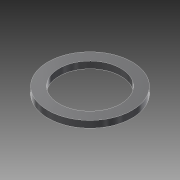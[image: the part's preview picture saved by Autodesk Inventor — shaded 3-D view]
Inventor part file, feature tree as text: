
AUTODESK INVENTOR PART (.ipt)
format: ipt  version: 2021.3 (Build 253353000, 353)  size: 99,328 bytes
history: native  units: mm
features: other x1, extrude x1, sketch x1
ambient origin geometry x8: Origin, YZ Plane, XZ Plane, XY Plane, X Axis, Y Axis, Z Axis, Center Point
bodies: Body1 (feature_tree)
feature tree (3):
  other  "Твердое тело1"
  extrude  "Выдавливание1"  Depth=8.2mm
  sketch  "Эскиз1"
